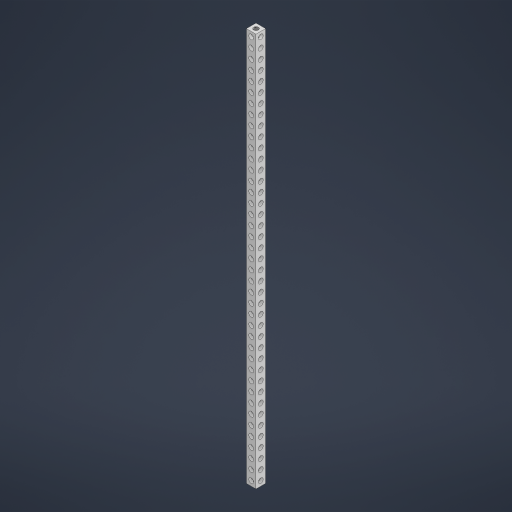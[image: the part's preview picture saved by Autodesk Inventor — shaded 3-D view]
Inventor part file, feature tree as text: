
AUTODESK INVENTOR PART (.ipt)
format: ipt  version: 2023 (Build 270158000, 158)  size: 1,368,064 bytes
history: native  units: in
note: dims shown in document units (in); Inventor stores cm internally (conversion verified against a paired STEP export)
features: mirror x1
ambient origin geometry x8: Origin, YZ Plane, XZ Plane, XY Plane, X Axis, Y Axis, Z Axis, Center Point
bodies: Solid1 (feature_tree)
feature tree (1):
  mirror  "Mirror3"
